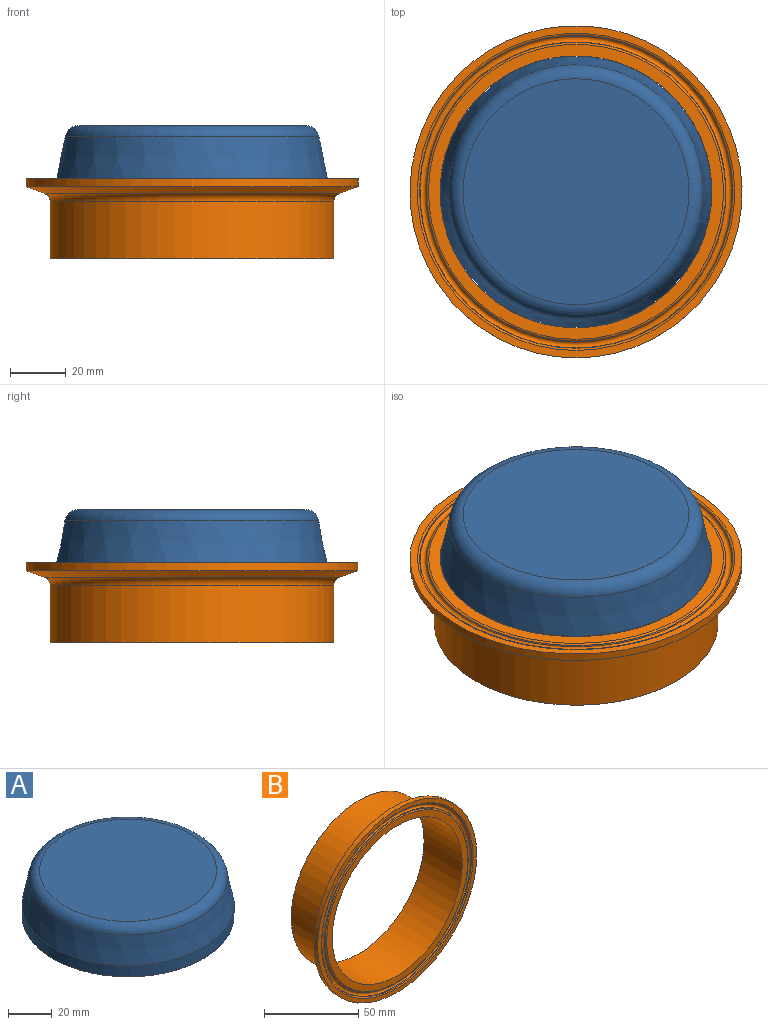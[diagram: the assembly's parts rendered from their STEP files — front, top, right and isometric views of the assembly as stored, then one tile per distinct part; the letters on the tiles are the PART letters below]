
ASSEMBLY  parts=2 mates=1
PART A: 5 faces, bbox 98.6x98.6x25.4 mm
  f0: cylinder r=48.45mm len=96.9mm, axis (0,0,-1), area 1933.1mm2, adj f2,f3
  f1: plane 80.95x80.95mm, normal (0,0,1), area 5146.9mm2, adj f4
  f2: plane 96.9x96.9mm, normal (0,0,-1), area 7374.7mm2, adj f0
  f3: cone r=44.64mm half-angle=11.3deg, axis (0,0,-1), area 4502.8mm2, adj f0,f4
  f4: torus R=40.48mm, axis (0,0,1), area 1904.7mm2, adj f1,f3
PART B: 13 faces, bbox 122.9x28.6x122.9 mm
  f0: cylinder r=59.46mm len=118.92mm, axis (0,-1,0), area 1062.8mm2, adj f1,f10
  f1: cone r=52.89mm half-angle=70deg, axis (0,-1,0), area 2468.6mm2, adj f0,f2
  f2: torus R=53.98mm, axis (0,-1,0), area 1256mm2, adj f1,f3
  f3: cylinder r=50.8mm len=101.6mm, axis (0,-1,0), area 6496.9mm2, adj f2,f12
  f4: cylinder r=48.69mm len=97.38mm, axis (0,-1,0), area 8742.2mm2, adj f11,f12
  f5: torus R=52.81mm, axis (0,-1,0), area 307.9mm2, adj f6,f11
  f6: cone r=53.7mm half-angle=23deg, axis (0,1,0), area 143.9mm2, adj f5,f7
  f7: torus R=54.8mm, axis (0,-1,0), area 961.3mm2, adj f6,f8
  f8: cone r=56.07mm half-angle=23deg, axis (0,-1,0), area 150.2mm2, adj f7,f9
  f9: torus R=56.79mm, axis (0,-1,0), area 326.2mm2, adj f8,f10
  f10: plane 118.92x118.92mm, normal (0,-1,0), area 975.3mm2, adj f0,f9
  f11: plane 105.62x105.62mm, normal (0,-1,0), area 1313.2mm2, adj f4,f5
  f12: plane 101.6x101.6mm, normal (0,1,0), area 658.9mm2, adj f3,f4
PLACE A t=(53.63,52.91,21.32)mm
PLACE B rot(axis=(-0.58,0.58,-0.58),120deg) t=(53.63,52.91,27.67)mm
MATE fastened A.f0 <-> B.f0  axis (0,0,1) through (53.63,52.91,27.67)mm
